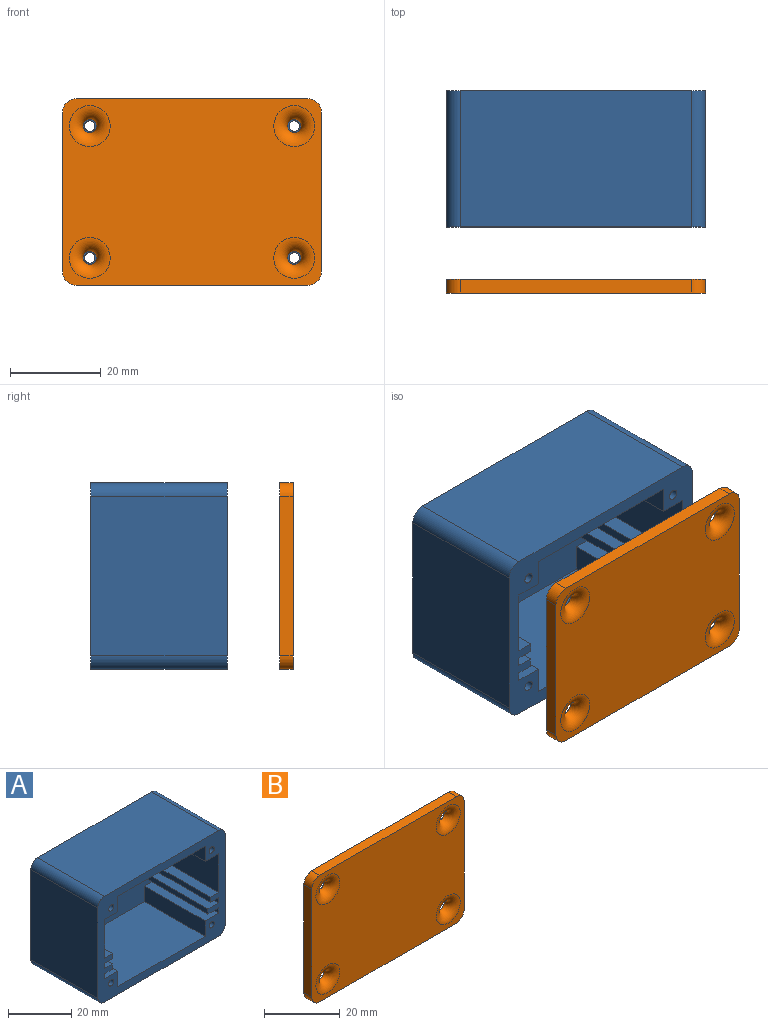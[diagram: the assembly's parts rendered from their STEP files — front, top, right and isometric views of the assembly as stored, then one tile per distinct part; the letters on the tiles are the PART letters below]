
ASSEMBLY  parts=2 mates=1
PART A: 43 faces, bbox 57x30x41 mm
  f0: plane 27x3.69mm, normal (0,0,-1), area 99.6mm2, adj f2,f3,f15,f42
  f1: plane 27x3.69mm, normal (0,0,1), area 99.6mm2, adj f2,f3,f5,f42
  f2: plane 27x2mm, normal (-1,0,0), area 54mm2, adj f0,f1,f3,f42
  f3: plane 57x41mm, normal (0,-1,0), area 703mm2, adj f0,f1,f2,f5,f6,f7,f8,f9
  f4: plane 57x41mm, normal (0,1,0), area 2312.7mm2, adj f11,f13,f17,f21,f25,f26,f27,f28
  f5: plane 27x15mm, normal (-1,0,0), area 405mm2, adj f1,f3,f10,f42
  f6: plane 27x2mm, normal (1,0,0), area 54mm2, adj f3,f38,f39,f42
  f7: plane 27x2mm, normal (1,0,0), area 54mm2, adj f3,f22,f36,f42
  f8: plane 27x2mm, normal (-1,0,0), area 54mm2, adj f3,f12,f33,f42
  f9: plane 27x6mm, normal (-1,0,0), area 162mm2, adj f3,f10,f19,f42
  f10: plane 27x6mm, normal (0,0,-1), area 162mm2, adj f3,f5,f9,f42
  f11: cylinder r=1.15mm len=30mm, axis (0,1,0), area 216.8mm2, adj f3,f4
  f12: plane 27x6mm, normal (0,0,1), area 162mm2, adj f3,f8,f14,f42
  f13: cylinder r=1.15mm len=30mm, axis (0,1,0), area 216.8mm2, adj f3,f4
  f14: plane 27x6mm, normal (-1,0,0), area 162mm2, adj f3,f12,f24,f42
  f15: plane 27x2mm, normal (-1,0,0), area 54mm2, adj f0,f3,f34,f42
  f16: plane 27x6mm, normal (0,0,-1), area 162mm2, adj f3,f18,f23,f42
  f17: cylinder r=1.15mm len=30mm, axis (0,1,0), area 216.8mm2, adj f3,f4
  f18: plane 27x6mm, normal (1,0,0), area 162mm2, adj f3,f16,f19,f42
  f19: plane 39x27mm, normal (0,0,-1), area 1053mm2, adj f3,f9,f18,f42
  f20: plane 27x6mm, normal (1,0,0), area 162mm2, adj f3,f22,f24,f42
  f21: cylinder r=1.15mm len=30mm, axis (0,1,0), area 216.8mm2, adj f3,f4
  f22: plane 27x6mm, normal (0,0,1), area 162mm2, adj f3,f7,f20,f42
  f23: plane 27x15mm, normal (1,0,0), area 405mm2, adj f3,f16,f41,f42
  f24: plane 39x27mm, normal (0,0,1), area 1053mm2, adj f3,f14,f20,f42
  f25: plane 51x30mm, normal (0,0,-1), area 1530mm2, adj f3,f4,f26,f32
  f26: cylinder r=3mm len=30mm, axis (0,1,0), area 141.4mm2, adj f3,f4,f25,f27
  f27: plane 35x30mm, normal (1,0,0), area 1050mm2, adj f3,f4,f26,f28
  f28: cylinder r=3mm len=30mm, axis (0,1,0), area 141.4mm2, adj f3,f4,f27,f29
  f29: plane 51x30mm, normal (0,0,1), area 1530mm2, adj f3,f4,f28,f30
  f30: cylinder r=3mm len=30mm, axis (0,1,0), area 141.4mm2, adj f3,f4,f29,f31
  f31: plane 35x30mm, normal (-1,0,0), area 1050mm2, adj f3,f4,f30,f32
  f32: cylinder r=3mm len=30mm, axis (0,1,0), area 141.4mm2, adj f3,f4,f25,f31
  f33: plane 27x4.72mm, normal (0,0,-1), area 127.6mm2, adj f3,f8,f35,f42
  f34: plane 27x4.72mm, normal (0,0,1), area 127.6mm2, adj f3,f15,f35,f42
  f35: plane 27x2mm, normal (-1,0,0), area 54mm2, adj f3,f33,f34,f42
  f36: plane 27x3.55mm, normal (0,0,-1), area 96mm2, adj f3,f7,f37,f42
  f37: plane 27x2mm, normal (1,0,0), area 54mm2, adj f3,f36,f38,f42
  f38: plane 27x3.55mm, normal (0,0,1), area 96mm2, adj f3,f6,f37,f42
  f39: plane 27x3.69mm, normal (0,0,-1), area 99.7mm2, adj f3,f6,f40,f42
  f40: plane 27x2mm, normal (1,0,0), area 54mm2, adj f3,f39,f41,f42
  f41: plane 27x3.69mm, normal (0,0,1), area 99.7mm2, adj f3,f23,f40,f42
  f42: plane 51x35mm, normal (0,-1,0), area 1609.7mm2, adj f0,f1,f2,f5,f6,f7,f8,f9
PART B: 14 faces, bbox 59.4x5.1x43.4 mm
  f0: plane 35x3mm, normal (1,0,0), area 105mm2, adj f1,f7,f8,f9
  f1: cylinder r=3mm len=3mm, axis (0,1,0), area 14.1mm2, adj f0,f2,f8,f9
  f2: plane 51x3mm, normal (0,0,1), area 153mm2, adj f1,f3,f8,f9
  f3: cylinder r=3mm len=3mm, axis (0,1,0), area 14.1mm2, adj f2,f4,f8,f9
  f4: plane 35x3mm, normal (-1,0,0), area 105mm2, adj f3,f5,f8,f9
  f5: cylinder r=3mm len=3mm, axis (0,1,0), area 14.1mm2, adj f4,f6,f8,f9
  f6: plane 51x3mm, normal (0,0,-1), area 153mm2, adj f5,f7,f8,f9
  f7: cylinder r=3mm len=3mm, axis (0,1,0), area 14.1mm2, adj f0,f6,f8,f9
  f8: plane 57x41mm, normal (0,-1,0), area 2074.8mm2, adj f0,f1,f2,f3,f4,f5,f6,f7
  f9: plane 57x41mm, normal (0,1,0), area 2301mm2, adj f0,f1,f2,f3,f4,f5,f6,f7
  f10: torus R=4.5mm, axis (0,-1,0), area 76.7mm2, adj f8,f9
  f11: torus R=4.5mm, axis (0,-1,0), area 76.7mm2, adj f8,f9
  f12: torus R=4.5mm, axis (0,-1,0), area 76.7mm2, adj f8,f9
  f13: torus R=4.5mm, axis (0,-1,0), area 76.7mm2, adj f8,f9
PLACE A t=(57.67,-54.71,-71)mm
PLACE B t=(54.67,-96.24,-74)mm
MATE slider A.f11 <-> B.f10  axis (0,-1,0) through (105.67,-84.71,-39)mm
